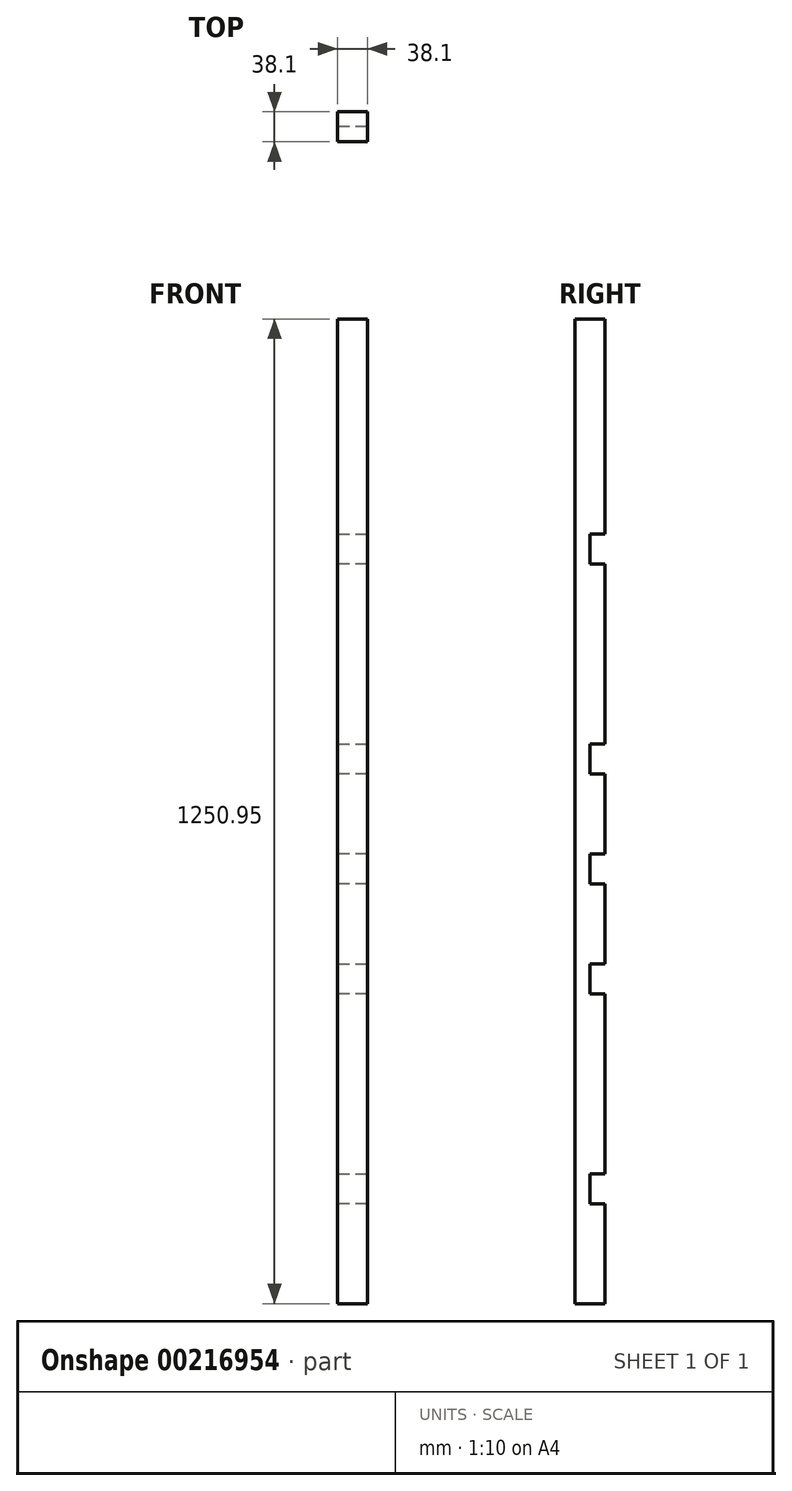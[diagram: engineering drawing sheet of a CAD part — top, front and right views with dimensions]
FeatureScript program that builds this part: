
annotation { "Feature Type Name" : "Feature", "Feature Type Description" : "" }
export const myFeature = defineFeature(function(context is Context, id is Id, definition is map)
    precondition{}
    {
        {
            var Q0;
            Q0=qCreatedBy(makeId("Top.planeOp"),FACE);
            var sketch = newSketch(context, id + "F0", { "sketchPlane" : qUnion([Q0])});
            skLineSegment(sketch, "E0", {"start": v(0, 0) * mm, "end": v(-50.8, 0) * mm});
            skLineSegment(sketch, "E1", {"start": v(0, 0) * mm, "end": v(50.8, 0) * mm});
            skLineSegment(sketch, "E2", {"start": v(50.8, 0) * mm, "end": v(50.8, 38.1) * mm});
            skLineSegment(sketch, "E3", {"start": v(88.9, 38.1) * mm, "end": v(88.9, 0) * mm});
            skLineSegment(sketch, "E4", {"start": v(88.9, 0) * mm, "end": v(317.5, 0) * mm});
            skLineSegment(sketch, "E5", {"start": v(317.5, 0) * mm, "end": v(317.5, 38.1) * mm});
            skLineSegment(sketch, "E6", {"start": v(355.6, 38.1) * mm, "end": v(355.6, 0) * mm});
            skLineSegment(sketch, "E7", {"start": v(355.6, 0) * mm, "end": v(628.65, 0) * mm});
            skLineSegment(sketch, "E8", {"start": v(628.65, 0) * mm, "end": v(628.65, 38.1) * mm});
            skLineSegment(sketch, "E9", {"start": v(-50.8, 0) * mm, "end": v(-50.8, 38.1) * mm});
            skLineSegment(sketch, "E10", {"start": v(-88.9, 38.1) * mm, "end": v(-190.5, 38.1) * mm});
            skLineSegment(sketch, "E11", {"start": v(-190.5, 38.1) * mm, "end": v(-190.5, 0) * mm});
            skLineSegment(sketch, "E12", {"start": v(-228.6, 0) * mm, "end": v(-228.6, 38.1) * mm});
            skLineSegment(sketch, "E13", {"start": v(-228.6, 38.1) * mm, "end": v(-457.2, 38.1) * mm});
            skLineSegment(sketch, "E14", {"start": v(-457.2, 38.1) * mm, "end": v(-457.2, 0) * mm});
            skLineSegment(sketch, "E15", {"start": v(-495.3, 0) * mm, "end": v(-495.3, 38.1) * mm});
            skLineSegment(sketch, "E16", {"start": v(-495.3, 38.1) * mm, "end": v(-622.3, 38.1) * mm});
            skLineSegment(sketch, "E17", {"start": v(-622.3, 38.1) * mm, "end": v(-622.3, 0) * mm});
            skLineSegment(sketch, "E18", {"start": v(-88.9, 0) * mm, "end": v(-88.9, 38.1) * mm});
            skLineSegment(sketch, "E19.trimOffspring", {"start": v(-622.3, 38.1) * mm, "end": v(-495.3, 38.1) * mm});
            skLineSegment(sketch, "E20.trimOffspring", {"start": v(-457.2, 38.1) * mm, "end": v(-228.6, 38.1) * mm});
            skLineSegment(sketch, "E21.trimOffspring", {"start": v(-190.5, 38.1) * mm, "end": v(-88.9, 38.1) * mm});
            skLineSegment(sketch, "E22.trimOffspring", {"start": v(-495.3, 0) * mm, "end": v(-622.3, 0) * mm});
            skLineSegment(sketch, "E23.trimOffspring", {"start": v(-228.6, 0) * mm, "end": v(-457.2, 0) * mm});
            skLineSegment(sketch, "E24.trimOffspring", {"start": v(-88.9, 0) * mm, "end": v(-190.5, 0) * mm});
            skLineSegment(sketch, "E25.trimOffspring", {"start": v(-50.8, 38.1) * mm, "end": v(50.8, 38.1) * mm});
            skLineSegment(sketch, "E26.trimOffspring", {"start": v(50.8, 0) * mm, "end": v(0, 0) * mm});
            skLineSegment(sketch, "E27.trimOffspring", {"start": v(88.9, 38.1) * mm, "end": v(317.5, 38.1) * mm});
            skLineSegment(sketch, "E28.trimOffspring", {"start": v(317.5, 0) * mm, "end": v(88.9, 0) * mm});
            skLineSegment(sketch, "E29.trimOffspring", {"start": v(355.6, 38.1) * mm, "end": v(628.65, 38.1) * mm});
            skLineSegment(sketch, "E30.trimOffspring", {"start": v(628.65, 0) * mm, "end": v(355.6, 0) * mm});
            skSolve(sketch);
        }
        {
            var Q0;
            Q0 = qSketchRegion(id + "F0", true);
            extrude(context, id + "F1", {"entities" : qUnion([Q0]), "depth" : 19.05 * mm});
        }
        {
            var Q0;
            Q0=makeQuery(id+"F1.opExtrude","CAP_FACE",FACE,{"disambiguationData":[OSD([sQuery(id+"F0.wireOp",EDGE,"E15"),sQuery(id+"F0.wireOp",EDGE,"E17"),sQuery(id+"F0.wireOp",EDGE,"E19.trimOffspring"),sQuery(id+"F0.wireOp",EDGE,"E22.trimOffspring")])],"isStart":false});
            var sketch = newSketch(context, id + "F2", { "sketchPlane" : qUnion([Q0])});
            skLineSegment(sketch, "E31.bottom", {"start": v(-622.3, 38.1) * mm, "end": v(628.65, 38.1) * mm});
            skLineSegment(sketch, "E31.top", {"start": v(-622.3, 0) * mm, "end": v(628.65, 0) * mm});
            skLineSegment(sketch, "E31.left", {"start": v(-622.3, 38.1) * mm, "end": v(-622.3, 0) * mm});
            skLineSegment(sketch, "E31.right", {"start": v(628.65, 38.1) * mm, "end": v(628.65, 0) * mm});
            skSolve(sketch);
        }
        {
            var Q0;
            Q0 = qSketchRegion(id + "F2", true);
            extrude(context, id + "F3", {"entities" : qUnion([Q0]), "depth" : 19.05 * mm});
        }
        {
            var Q0;
            Q0=makeQuery(id+"F3.opExtrude","SWEPT_BODY",BODY,{"disambiguationData":[OSD([sQuery(id+"F2.wireOp",EDGE,"E31.bottom"),sQuery(id+"F2.wireOp",EDGE,"E31.top"),sQuery(id+"F2.wireOp",EDGE,"E31.left"),sQuery(id+"F2.wireOp",EDGE,"E31.right")])]});
            var Q1;
            Q1=makeQuery(id+"F1.opExtrude","SWEPT_BODY",BODY,{"disambiguationData":[OSD([sQuery(id+"F0.wireOp",EDGE,"E2"),sQuery(id+"F0.wireOp",EDGE,"E0"),sQuery(id+"F0.wireOp",EDGE,"E9"),sQuery(id+"F0.wireOp",EDGE,"E25.trimOffspring"),sQuery(id+"F0.wireOp",EDGE,"E26.trimOffspring")])]});
            var Q2;
            Q2=makeQuery(id+"F1.opExtrude","SWEPT_BODY",BODY,{"disambiguationData":[OSD([sQuery(id+"F0.wireOp",EDGE,"E3"),sQuery(id+"F0.wireOp",EDGE,"E5"),sQuery(id+"F0.wireOp",EDGE,"E27.trimOffspring"),sQuery(id+"F0.wireOp",EDGE,"E28.trimOffspring")])]});
            var Q3;
            Q3=makeQuery(id+"F1.opExtrude","SWEPT_BODY",BODY,{"disambiguationData":[OSD([sQuery(id+"F0.wireOp",EDGE,"E6"),sQuery(id+"F0.wireOp",EDGE,"E8"),sQuery(id+"F0.wireOp",EDGE,"E29.trimOffspring"),sQuery(id+"F0.wireOp",EDGE,"E30.trimOffspring")])]});
            var Q4;
            Q4=makeQuery(id+"F1.opExtrude","SWEPT_BODY",BODY,{"disambiguationData":[OSD([sQuery(id+"F0.wireOp",EDGE,"E11"),sQuery(id+"F0.wireOp",EDGE,"E18"),sQuery(id+"F0.wireOp",EDGE,"E21.trimOffspring"),sQuery(id+"F0.wireOp",EDGE,"E24.trimOffspring")])]});
            var Q5;
            Q5=makeQuery(id+"F1.opExtrude","SWEPT_BODY",BODY,{"disambiguationData":[OSD([sQuery(id+"F0.wireOp",EDGE,"E12"),sQuery(id+"F0.wireOp",EDGE,"E14"),sQuery(id+"F0.wireOp",EDGE,"E20.trimOffspring"),sQuery(id+"F0.wireOp",EDGE,"E23.trimOffspring")])]});
            var Q6;
            Q6=makeQuery(id+"F1.opExtrude","SWEPT_BODY",BODY,{"disambiguationData":[OSD([sQuery(id+"F0.wireOp",EDGE,"E15"),sQuery(id+"F0.wireOp",EDGE,"E17"),sQuery(id+"F0.wireOp",EDGE,"E19.trimOffspring"),sQuery(id+"F0.wireOp",EDGE,"E22.trimOffspring")])]});
            booleanBodies(context, id + "F4", {"operationType" : BooleanOperationType.UNION, "tools" : qUnion([Q0, Q1, Q2, Q3, Q4, Q5, Q6])});
        }
        {
            var Q0;
            Q0=makeQuery(id+"F3.opExtrude","SWEPT_BODY",BODY,{"disambiguationData":[OSD([sQuery(id+"F2.wireOp",EDGE,"E31.bottom"),sQuery(id+"F2.wireOp",EDGE,"E31.top"),sQuery(id+"F2.wireOp",EDGE,"E31.left"),sQuery(id+"F2.wireOp",EDGE,"E31.right")])]});
            var Q1;
            Q1=makeQuery(id+"F3.opExtrude","CAP_EDGE",EDGE,{"disambiguationData":[OSD([sQuery(id+"F2.wireOp",EDGE,"E31.left")])],"isStart":false});
            transform(context, id + "F5", {"entities" : qUnion([Q0]), "transformType" : TransformType.ROTATION, "transformAxis" : qUnion([Q1]), "angle" : 90 * degree, "makeCopy" : false});
        }
        {
            var Q0;
            Q0=makeQuery(id+"F3.opExtrude","SWEPT_BODY",BODY,{"disambiguationData":[OSD([sQuery(id+"F2.wireOp",EDGE,"E31.bottom"),sQuery(id+"F2.wireOp",EDGE,"E31.top"),sQuery(id+"F2.wireOp",EDGE,"E31.left"),sQuery(id+"F2.wireOp",EDGE,"E31.right")])]});
            var Q1;
            Q1=makeQuery(id+"F3.opExtrude","CAP_EDGE",EDGE,{"disambiguationData":[OSD([sQuery(id+"F2.wireOp",EDGE,"E31.bottom")])],"isStart":false});
            transform(context, id + "F6", {"entities" : qUnion([Q0]), "transformType" : TransformType.ROTATION, "transformAxis" : qUnion([Q1]), "angle" : 90 * degree, "makeCopy" : false});
        }
    });
